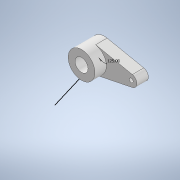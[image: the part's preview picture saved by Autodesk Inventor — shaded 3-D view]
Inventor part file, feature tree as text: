
AUTODESK INVENTOR PART (.ipt)
format: ipt  version: 2020 (Build 240168000, 168)  size: 127,488 bytes
history: native  units: mm
features: sketch x3, extrude x2, projected_geometry x1
ambient origin geometry x8: Origin, YZ Plane, XZ Plane, XY Plane, X Axis, Y Axis, Z Axis, Center Point
bodies: Solid1 (feature_tree)
feature tree (6):
  extrude  "Extrusion1"  Depth=7.0mm
  extrude  "Extrusion2"  Depth=3.0mm
  sketch  "Sketch3"  dims[d4=10.0mm d5=3.0mm d6=0.0mm d7=3.0mm d8=0.0mm d9=21.816616mm]
  sketch  "Sketch1"  dims[d0=3.4mm d1=7.0mm]
  sketch  "Sketch2"  dims[d2=3.0mm d3=1.0mm]
  projected_geometry  "Projected Loop1"
